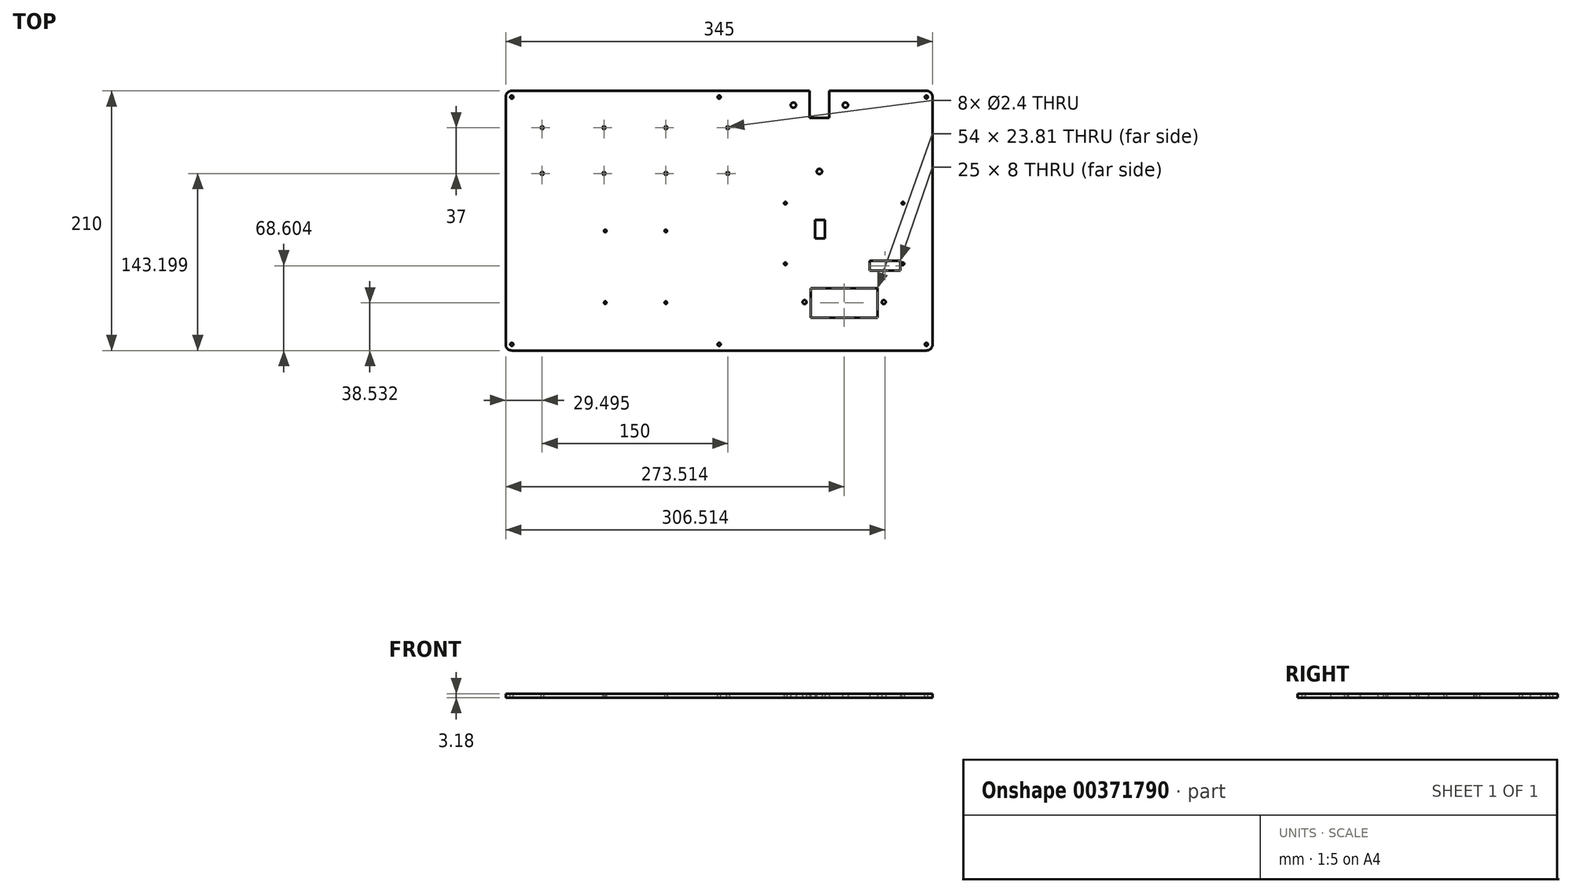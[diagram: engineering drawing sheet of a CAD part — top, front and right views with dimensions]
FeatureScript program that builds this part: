
annotation { "Feature Type Name" : "Feature", "Feature Type Description" : "" }
export const myFeature = defineFeature(function(context is Context, id is Id, definition is map)
    precondition{}
    {
        {
            var Q0;
            Q0=qCreatedBy(makeId("Top.planeOp"),FACE);
            var sketch = newSketch(context, id + "F0", { "sketchPlane" : qUnion([Q0])});
            skLineSegment(sketch, "E0.bottom", {"start": v(0, 0) * mm, "end": v(345, 0) * mm});
            skLineSegment(sketch, "E0.top", {"start": v(0, 210) * mm, "end": v(345, 210) * mm});
            skLineSegment(sketch, "E0.left", {"start": v(0, 0) * mm, "end": v(0, 210) * mm});
            skLineSegment(sketch, "E0.right", {"start": v(345, 0) * mm, "end": v(345, 210) * mm});
            skLineSegment(sketch, "E1.bottom", {"start": v(80.44, 96.73) * mm, "end": v(129.44, 96.73) * mm, "construction": true});
            skLineSegment(sketch, "E1.top", {"start": v(80.44, 38.73) * mm, "end": v(129.44, 38.73) * mm, "construction": true});
            skLineSegment(sketch, "E1.left", {"start": v(80.44, 96.73) * mm, "end": v(80.44, 38.73) * mm, "construction": true});
            skLineSegment(sketch, "E1.right", {"start": v(129.44, 96.73) * mm, "end": v(129.44, 38.73) * mm, "construction": true});
            skLineSegment(sketch, "E2.top", {"start": v(80.44, 13.73) * mm, "end": v(129.44, 13.73) * mm, "construction": true});
            skLineSegment(sketch, "E2.left", {"start": v(80.44, 38.73) * mm, "end": v(80.44, 13.73) * mm, "construction": true});
            skLineSegment(sketch, "E2.right", {"start": v(129.44, 38.73) * mm, "end": v(129.44, 13.73) * mm, "construction": true});
            skLineSegment(sketch, "E3.bottom", {"start": v(226.01, 55.16) * mm, "end": v(321.01, 55.16) * mm, "construction": true});
            skLineSegment(sketch, "E3.top", {"start": v(226.01, 23.16) * mm, "end": v(321.01, 23.16) * mm, "construction": true});
            skLineSegment(sketch, "E3.left", {"start": v(226.01, 55.16) * mm, "end": v(226.01, 23.16) * mm, "construction": true});
            skLineSegment(sketch, "E3.right", {"start": v(321.01, 55.16) * mm, "end": v(321.01, 23.16) * mm, "construction": true});
            skLineSegment(sketch, "E4", {"start": v(241.51, 39.16) * mm, "end": v(305.51, 39.16) * mm, "construction": true});
            skPoint(sketch, "E4.startSnap0", {"position": v(226.01, 39.16) * mm});
            skLineSegment(sketch, "E5", {"start": v(273.51, 55.16) * mm, "end": v(273.51, 39.16) * mm, "construction": true});
            skLineSegment(sketch, "E6", {"start": v(226.01, 39.16) * mm, "end": v(241.51, 39.16) * mm, "construction": true});
            skLineSegment(sketch, "E7", {"start": v(305.51, 39.16) * mm, "end": v(321.01, 39.16) * mm, "construction": true});
            skCircle(sketch, "E8", {"center": v(305.51, 39.16) * mm, "radius": 1.6 * mm});
            skCircle(sketch, "E9", {"center": v(241.51, 39.16) * mm, "radius": 1.6 * mm});
            skLineSegment(sketch, "E10.bottom", {"start": v(226.01, 119.16) * mm, "end": v(321.01, 119.16) * mm, "construction": true});
            skLineSegment(sketch, "E10.top", {"start": v(226.01, 70.16) * mm, "end": v(321.01, 70.16) * mm, "construction": true});
            skLineSegment(sketch, "E10.left", {"start": v(226.01, 119.16) * mm, "end": v(226.01, 70.16) * mm, "construction": true});
            skLineSegment(sketch, "E10.right", {"start": v(321.01, 119.16) * mm, "end": v(321.01, 70.16) * mm, "construction": true});
            skCircle(sketch, "E11", {"center": v(226.01, 119.16) * mm, "radius": 1.02 * mm});
            skCircle(sketch, "E12", {"center": v(226.01, 70.16) * mm, "radius": 1.02 * mm});
            skCircle(sketch, "E13", {"center": v(321.01, 70.16) * mm, "radius": 1.02 * mm});
            skCircle(sketch, "E14", {"center": v(321.01, 119.16) * mm, "radius": 1.02 * mm});
            skCircle(sketch, "E15", {"center": v(80.44, 96.73) * mm, "radius": 1.02 * mm});
            skCircle(sketch, "E16", {"center": v(80.44, 38.73) * mm, "radius": 1.02 * mm});
            skCircle(sketch, "E17", {"center": v(129.44, 38.73) * mm, "radius": 1.02 * mm});
            skCircle(sketch, "E18", {"center": v(129.44, 96.73) * mm, "radius": 1.02 * mm});
            skLineSegment(sketch, "E19", {"start": v(29.5, 180.2) * mm, "end": v(29.5, 143.2) * mm, "construction": true});
            skCircle(sketch, "E20", {"center": v(29.5, 143.2) * mm, "radius": 1.2 * mm});
            skCircle(sketch, "E21", {"center": v(29.5, 180.2) * mm, "radius": 1.2 * mm});
            skCircle(sketch, "E22.1.0.0", {"center": v(79.5, 180.2) * mm, "radius": 1.2 * mm});
            skCircle(sketch, "E22.1.0.1", {"center": v(79.5, 143.2) * mm, "radius": 1.2 * mm});
            skCircle(sketch, "E22.2.0.0", {"center": v(129.5, 180.2) * mm, "radius": 1.2 * mm});
            skCircle(sketch, "E22.2.0.1", {"center": v(129.5, 143.2) * mm, "radius": 1.2 * mm});
            skCircle(sketch, "E22.3.0.0", {"center": v(179.5, 180.2) * mm, "radius": 1.2 * mm});
            skCircle(sketch, "E22.3.0.1", {"center": v(179.5, 143.2) * mm, "radius": 1.2 * mm});
            skLineSegment(sketch, "E22.direction1", {"start": v(29.5, 180.2) * mm, "end": v(79.5, 180.2) * mm, "construction": true});
            skLineSegment(sketch, "E23", {"start": v(273.51, 55.16) * mm, "end": v(273.51, 70.16) * mm, "construction": true});
            skCircle(sketch, "E24", {"center": v(232.51, 198.5) * mm, "radius": 2.12 * mm});
            skCircle(sketch, "E25", {"center": v(274.51, 198.5) * mm, "radius": 2.12 * mm});
            skCircle(sketch, "E26", {"center": v(253.51, 144.8) * mm, "radius": 2.12 * mm});
            skLineSegment(sketch, "E27.bottom", {"start": v(226.01, 210) * mm, "end": v(282.01, 210) * mm, "construction": true});
            skLineSegment(sketch, "E27.top", {"start": v(226.01, 138) * mm, "end": v(282.01, 138) * mm, "construction": true});
            skLineSegment(sketch, "E27.left", {"start": v(226.01, 210) * mm, "end": v(226.01, 138) * mm, "construction": true});
            skLineSegment(sketch, "E27.right", {"start": v(282.01, 210) * mm, "end": v(282.01, 138) * mm, "construction": true});
            skLineSegment(sketch, "E28.bottom", {"start": v(246.51, 50.44) * mm, "end": v(300.51, 50.44) * mm});
            skLineSegment(sketch, "E28.top", {"start": v(246.51, 26.63) * mm, "end": v(300.51, 26.63) * mm});
            skLineSegment(sketch, "E28.left", {"start": v(246.51, 50.44) * mm, "end": v(246.51, 26.63) * mm});
            skLineSegment(sketch, "E28.right", {"start": v(300.51, 50.44) * mm, "end": v(300.51, 26.63) * mm});
            skLineSegment(sketch, "E29.bottom", {"start": v(245.51, 210) * mm, "end": v(261.51, 210) * mm});
            skLineSegment(sketch, "E29.top", {"start": v(245.51, 188) * mm, "end": v(261.51, 188) * mm});
            skLineSegment(sketch, "E29.left", {"start": v(245.51, 210) * mm, "end": v(245.51, 188) * mm});
            skLineSegment(sketch, "E29.right", {"start": v(261.51, 210) * mm, "end": v(261.51, 188) * mm});
            skLineSegment(sketch, "E30", {"start": v(253.51, 144.8) * mm, "end": v(253.51, 188) * mm, "construction": true});
            skLineSegment(sketch, "E31.bottom", {"start": v(294.01, 72.6) * mm, "end": v(319.01, 72.6) * mm});
            skLineSegment(sketch, "E31.top", {"start": v(294.01, 64.6) * mm, "end": v(319.01, 64.6) * mm});
            skLineSegment(sketch, "E31.left", {"start": v(294.01, 72.6) * mm, "end": v(294.01, 64.6) * mm});
            skLineSegment(sketch, "E31.right", {"start": v(319.01, 72.6) * mm, "end": v(319.01, 64.6) * mm});
            skLineSegment(sketch, "E32.bottom", {"start": v(250.01, 105.66) * mm, "end": v(258.01, 105.66) * mm});
            skLineSegment(sketch, "E32.top", {"start": v(250.01, 90.66) * mm, "end": v(258.01, 90.66) * mm});
            skLineSegment(sketch, "E32.left", {"start": v(250.01, 105.66) * mm, "end": v(250.01, 90.66) * mm});
            skLineSegment(sketch, "E32.right", {"start": v(258.01, 105.66) * mm, "end": v(258.01, 90.66) * mm});
            skPoint(sketch, "E33", {"position": v(254.01, 105.66) * mm});
            skPoint(sketch, "E34", {"position": v(250.01, 98.16) * mm});
            skSolve(sketch);
        }
        {
            var Q0;
            Q0=makeQuery(id+"F0.imprint","IMPRINT",FACE,{"disambiguationData":[TD([[makeQuery(id+"F0.imprint","IMPRINT",EDGE,{"derivedFrom":sQuery(id+"F0.wireOp",EDGE,"E0.bottom")}),1.0]])]});
            extrude(context, id + "F1", {"entities" : qUnion([Q0]), "depth" : 3.17 * mm});
        }
        {
            var Q0;
            Q0=makeQuery(id+"F1.opExtrude","SWEPT_EDGE",EDGE,{"disambiguationData":[OSD([sQuery(id+"F0.wireOp",EDGE,"E0.top"),sQuery(id+"F0.wireOp",EDGE,"E0.left")])]});
            var Q1;
            Q1=makeQuery(id+"F1.opExtrude","SWEPT_EDGE",EDGE,{"disambiguationData":[OSD([sQuery(id+"F0.wireOp",EDGE,"E0.bottom"),sQuery(id+"F0.wireOp",EDGE,"E0.left")])]});
            var Q2;
            Q2=makeQuery(id+"F1.opExtrude","SWEPT_EDGE",EDGE,{"disambiguationData":[OSD([sQuery(id+"F0.wireOp",EDGE,"E0.bottom"),sQuery(id+"F0.wireOp",EDGE,"E0.right")])]});
            var Q3;
            Q3=makeQuery(id+"F1.opExtrude","SWEPT_EDGE",EDGE,{"disambiguationData":[OSD([sQuery(id+"F0.wireOp",EDGE,"E0.top"),sQuery(id+"F0.wireOp",EDGE,"E0.right")])]});
            fillet(context, id + "F2", {"entities" : qUnion([Q0, Q1, Q2, Q3]), "radius" : 5 * mm, "tangentPropagation" : true, "allowEdgeOverflow" : false});
        }
        {
            var Q0;
            Q0=makeQuery(id+"F1.opExtrude","CAP_FACE",FACE,{"disambiguationData":[OSD([sQuery(id+"F0.wireOp",EDGE,"E0.bottom"),sQuery(id+"F0.wireOp",EDGE,"E0.top"),sQuery(id+"F0.wireOp",EDGE,"E0.left"),sQuery(id+"F0.wireOp",EDGE,"E0.right"),sQuery(id+"F0.wireOp",EDGE,"E8"),sQuery(id+"F0.wireOp",EDGE,"E9"),sQuery(id+"F0.wireOp",EDGE,"E11"),sQuery(id+"F0.wireOp",EDGE,"E12"),sQuery(id+"F0.wireOp",EDGE,"E13"),sQuery(id+"F0.wireOp",EDGE,"E14"),sQuery(id+"F0.wireOp",EDGE,"E15"),sQuery(id+"F0.wireOp",EDGE,"E16"),sQuery(id+"F0.wireOp",EDGE,"E17"),sQuery(id+"F0.wireOp",EDGE,"E18"),sQuery(id+"F0.wireOp",EDGE,"E20"),sQuery(id+"F0.wireOp",EDGE,"E21"),sQuery(id+"F0.wireOp",EDGE,"E22.1.0.0"),sQuery(id+"F0.wireOp",EDGE,"E22.1.0.1"),sQuery(id+"F0.wireOp",EDGE,"E22.2.0.0"),sQuery(id+"F0.wireOp",EDGE,"E22.2.0.1"),sQuery(id+"F0.wireOp",EDGE,"E22.3.0.0"),sQuery(id+"F0.wireOp",EDGE,"E22.3.0.1"),sQuery(id+"F0.wireOp",EDGE,"E24"),sQuery(id+"F0.wireOp",EDGE,"E25"),sQuery(id+"F0.wireOp",EDGE,"E26"),sQuery(id+"F0.wireOp",EDGE,"E28.bottom"),sQuery(id+"F0.wireOp",EDGE,"E28.top"),sQuery(id+"F0.wireOp",EDGE,"E28.left"),sQuery(id+"F0.wireOp",EDGE,"E28.right"),sQuery(id+"F0.wireOp",EDGE,"E29.top"),sQuery(id+"F0.wireOp",EDGE,"E29.left"),sQuery(id+"F0.wireOp",EDGE,"E29.right")])],"isStart":false});
            var sketch = newSketch(context, id + "F3", { "sketchPlane" : qUnion([Q0])});
            skCircle(sketch, "E35", {"center": v(5, 5) * mm, "radius": 1.25 * mm});
            skCircle(sketch, "E36", {"center": v(5, 205) * mm, "radius": 1.25 * mm});
            skCircle(sketch, "E37", {"center": v(340, 5) * mm, "radius": 1.25 * mm});
            skCircle(sketch, "E38", {"center": v(340, 205) * mm, "radius": 1.25 * mm});
            skCircle(sketch, "E39", {"center": v(172.5, 5) * mm, "radius": 1.25 * mm});
            skCircle(sketch, "E40", {"center": v(172.5, 205) * mm, "radius": 1.25 * mm});
            skLineSegment(sketch, "E41", {"start": v(172.5, 0) * mm, "end": v(172.5, 210) * mm, "construction": true});
            skSolve(sketch);
        }
        {
            var Q0;
            Q0 = qSketchRegion(id + "F3", true);
            extrude(context, id + "F4", {"entities" : qUnion([Q0]), "operationType" : NewBodyOperationType.REMOVE, "endBound" : BoundingType.THROUGH_ALL, "oppositeDirection" : true, "depth" : 25 * mm});
        }
    });
